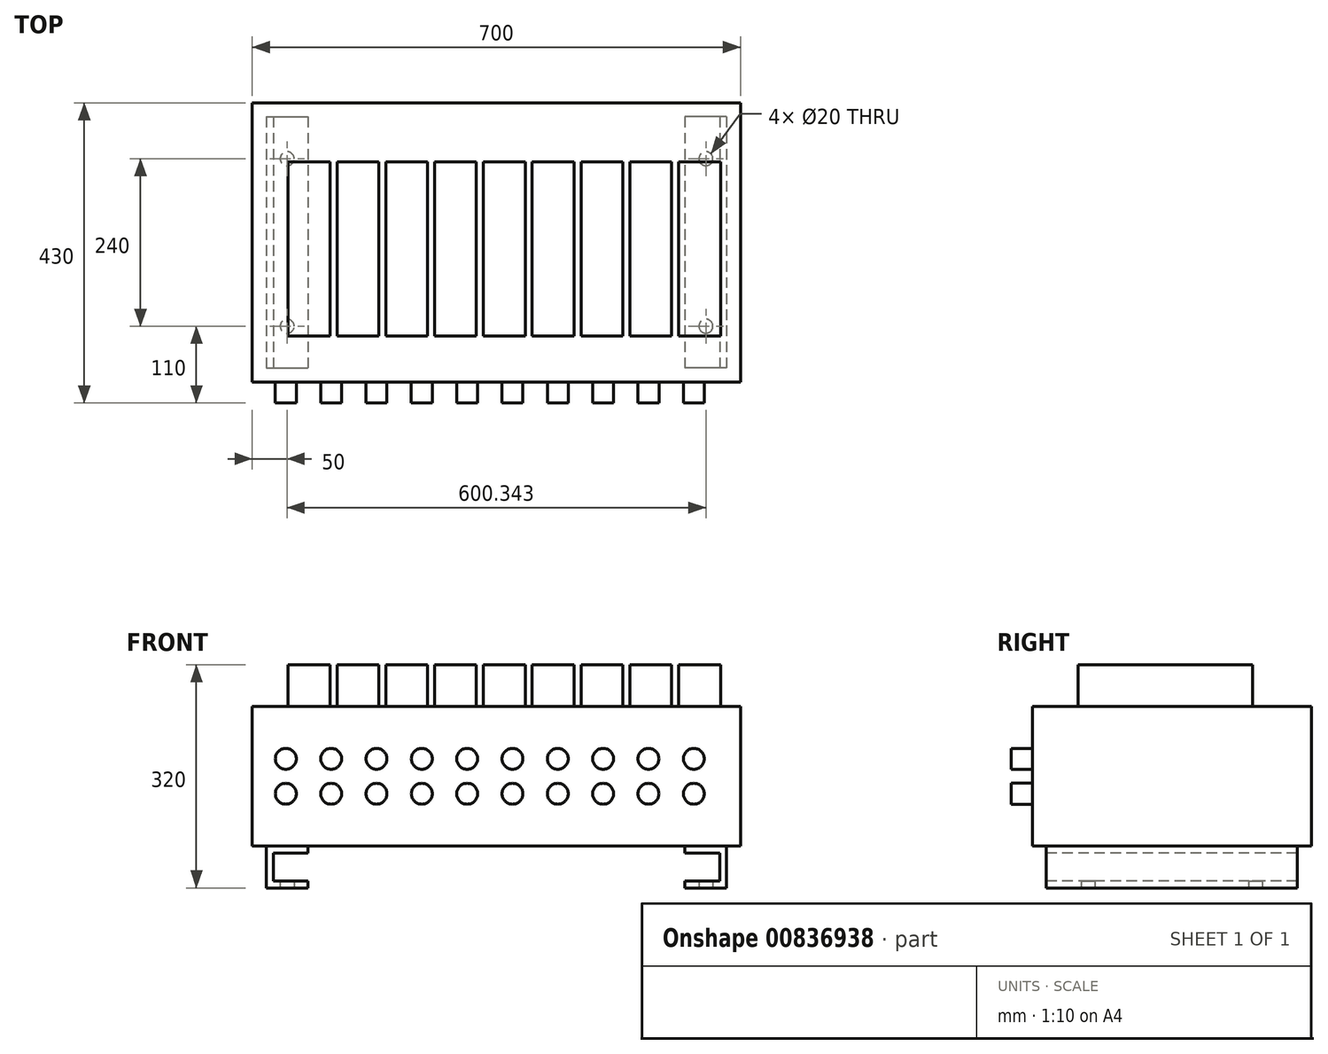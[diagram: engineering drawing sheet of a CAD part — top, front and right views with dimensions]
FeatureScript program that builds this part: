
annotation { "Feature Type Name" : "Feature", "Feature Type Description" : "" }
export const myFeature = defineFeature(function(context is Context, id is Id, definition is map)
    precondition{}
    {
        {
            var Q0;
            Q0=qCreatedBy(makeId("Front.planeOp"),FACE);
            var sketch = newSketch(context, id + "F0", { "sketchPlane" : qUnion([Q0])});
            skLineSegment(sketch, "E0.bottom", {"start": v(0, 0) * mm, "end": v(700, 0) * mm});
            skLineSegment(sketch, "E0.top", {"start": v(0, 200) * mm, "end": v(700, 200) * mm});
            skLineSegment(sketch, "E0.left", {"start": v(0, 0) * mm, "end": v(0, 200) * mm});
            skLineSegment(sketch, "E0.right", {"start": v(700, 0) * mm, "end": v(700, 200) * mm});
            skSolve(sketch);
        }
        {
            var Q0;
            Q0=makeQuery(id+"F0.imprint","IMPRINT",FACE,{"disambiguationData":[TD([[makeQuery(id+"F0.imprint","IMPRINT",EDGE,{"derivedFrom":sQuery(id+"F0.wireOp",EDGE,"E0.bottom")}),1.0]])]});
            extrude(context, id + "F1", {"entities" : qUnion([Q0]), "oppositeDirection" : true, "depth" : 400 * mm, "offsetDistance" : 25 * mm});
        }
        {
            var Q0;
            Q0=qCreatedBy(makeId("Front.planeOp"),FACE);
            cPlane(context, id + "F2", {"entities" : qUnion([Q0]), "cplaneType" : CPlaneType.OFFSET, "offset" : 20 * mm, "oppositeDirection" : true, "width" : 150 * mm, "height" : 150 * mm});
        }
        {
            var Q0;
            Q0=qCreatedBy(id+"F2.planeOp",FACE);
            var sketch = newSketch(context, id + "F3", { "sketchPlane" : qUnion([Q0])});
            skLineSegment(sketch, "E1", {"start": v(20, -19.14) * mm, "end": v(20, 199.88) * mm});
            skLineSegment(sketch, "E2.bottom", {"start": v(20, 0) * mm, "end": v(80, 0) * mm});
            skLineSegment(sketch, "E2.top", {"start": v(30, -10) * mm, "end": v(80, -10) * mm});
            skLineSegment(sketch, "E2.left", {"start": v(20, 0) * mm, "end": v(20, -10) * mm});
            skLineSegment(sketch, "E2.right", {"start": v(80, 0) * mm, "end": v(80, -10) * mm});
            skLineSegment(sketch, "E3.top", {"start": v(20, -60) * mm, "end": v(30, -60) * mm});
            skLineSegment(sketch, "E3.left", {"start": v(20, -10) * mm, "end": v(20, -60) * mm});
            skLineSegment(sketch, "E3.right", {"start": v(30, -10) * mm, "end": v(30, -50) * mm});
            skLineSegment(sketch, "E4.bottom", {"start": v(20, -60) * mm, "end": v(80, -60) * mm});
            skLineSegment(sketch, "E4.top", {"start": v(30, -50) * mm, "end": v(80, -50) * mm});
            skLineSegment(sketch, "E4.left", {"start": v(20, -60) * mm, "end": v(20, -50) * mm});
            skLineSegment(sketch, "E4.right", {"start": v(80, -60) * mm, "end": v(80, -50) * mm});
            skLineSegment(sketch, "E5", {"start": v(0, 0) * mm, "end": v(0, -147) * mm, "construction": true});
            skLineSegment(sketch, "E6", {"start": v(0, -147) * mm, "end": v(700, -147) * mm, "construction": true});
            skLineSegment(sketch, "E7", {"start": v(350, -147) * mm, "end": v(350, -185.28) * mm, "construction": true});
            skLineSegment(sketch, "E8.MirrorCS", {"start": v(680, 0) * mm, "end": v(680, -10) * mm});
            skLineSegment(sketch, "E9.MirrorCS", {"start": v(680, -60) * mm, "end": v(670, -60) * mm});
            skLineSegment(sketch, "E10.MirrorCS", {"start": v(620, -60) * mm, "end": v(620, -50) * mm});
            skLineSegment(sketch, "E11.MirrorCS", {"start": v(620, 0) * mm, "end": v(620, -10) * mm});
            skLineSegment(sketch, "E12.MirrorCS", {"start": v(670, -50) * mm, "end": v(620, -50) * mm});
            skLineSegment(sketch, "E13.MirrorCS", {"start": v(680, -10) * mm, "end": v(680, -60) * mm});
            skLineSegment(sketch, "E14.MirrorCS", {"start": v(670, -10) * mm, "end": v(670, -50) * mm});
            skLineSegment(sketch, "E15.MirrorCS", {"start": v(670, -10) * mm, "end": v(620, -10) * mm});
            skLineSegment(sketch, "E16.MirrorCS", {"start": v(680, 0) * mm, "end": v(620, 0) * mm});
            skLineSegment(sketch, "E17.MirrorCS", {"start": v(680, -60) * mm, "end": v(620, -60) * mm});
            skPoint(sketch, "E18.orphan", {"position": v(680, -50) * mm});
            skLineSegment(sketch, "E19", {"start": v(50, -60) * mm, "end": v(50, -71.61) * mm, "construction": true});
            skSolve(sketch);
        }
        {
            var Q0;
            Q0=makeQuery(id+"F3.imprint","IMPRINT",FACE,{"disambiguationData":[TD([[makeQuery(id+"F3.imprint","IMPRINT",EDGE,{"derivedFrom":sQuery(id+"F3.wireOp",EDGE,"E2.bottom")}),-1.0]])]});
            var Q1;
            {var subQ1=sQuery(id+"F3.wireOp",EDGE,"E3.bottom");Q1=makeQuery(id+"F3.imprint","IMPRINT",FACE,{"disambiguationData":[TD([[makeQuery(id+"F3.imprint","IMPRINT",EDGE,{"derivedFrom":subQ1}),-1.0]])]});}
            var Q2;
            {var subQ5=sQuery(id+"F3.wireOp",EDGE,"E4.left");Q2=makeQuery(id+"F3.imprint","IMPRINT",FACE,{"disambiguationData":[TD([[makeQuery(id+"F3.imprint","IMPRINT",EDGE,{"derivedFrom":subQ5}),-1.0]])]});}
            var Q3;
            {var subQ5=sQuery(id+"F3.wireOp",EDGE,"E4.right");Q3=makeQuery(id+"F3.imprint","IMPRINT",FACE,{"disambiguationData":[TD([[makeQuery(id+"F3.imprint","IMPRINT",EDGE,{"derivedFrom":subQ5}),1.0]])]});}
            var Q4;
            {var subQ1=sQuery(id+"F3.wireOp",EDGE,"E8.MirrorCS");Q4=makeQuery(id+"F3.imprint","IMPRINT",FACE,{"disambiguationData":[TD([[makeQuery(id+"F3.imprint","IMPRINT",EDGE,{"derivedFrom":subQ1}),-1.0]])]});}
            var Q5;
            {var subQ0=sQuery(id+"F3.wireOp",EDGE,"E13.MirrorCS");var subQ1=sQuery(id+"F3.wireOp",EDGE,"E12.MirrorCS");var subQ2=makeQuery(id+"F3.imprint","INTERSECT",VERTEX,{"derivedFrom":[subQ1,subQ0]});Q5=makeQuery(id+"F3.imprint","IMPRINT",FACE,{"disambiguationData":[TD([[makeQuery(id+"F3.imprint","IMPRINT",EDGE,{"disambiguationData":[TD([[subQ2,-1.0]])],"derivedFrom":subQ1}),-1.0]])]});}
            var Q6;
            {var subQ0=sQuery(id+"F3.wireOp",EDGE,"E10.MirrorCS");Q6=makeQuery(id+"F3.imprint","IMPRINT",FACE,{"disambiguationData":[TD([[makeQuery(id+"F3.imprint","IMPRINT",EDGE,{"derivedFrom":subQ0}),-1.0]])]});}
            var Q7;
            {var subQ0=sQuery(id+"F3.wireOp",EDGE,"E13.MirrorCS");var subQ1=sQuery(id+"F3.wireOp",EDGE,"E12.MirrorCS");var subQ2=makeQuery(id+"F3.imprint","INTERSECT",VERTEX,{"derivedFrom":[subQ1,subQ0]});Q7=makeQuery(id+"F3.imprint","IMPRINT",FACE,{"disambiguationData":[TD([[makeQuery(id+"F3.imprint","IMPRINT",EDGE,{"disambiguationData":[TD([[subQ2,-1.0]])],"derivedFrom":subQ1}),1.0]])]});}
            extrude(context, id + "F4", {"entities" : qUnion([Q0, Q1, Q2, Q3, Q4, Q5, Q6, Q7]), "operationType" : NewBodyOperationType.ADD, "oppositeDirection" : true, "depth" : 360 * mm, "offsetDistance" : 25 * mm});
        }
        {
            var Q0;
            Q0=makeQuery(id+"F1.opExtrude","CAP_FACE",FACE,{"disambiguationData":[OSD([sQuery(id+"F0.wireOp",EDGE,"E0.bottom"),sQuery(id+"F0.wireOp",EDGE,"E0.top"),sQuery(id+"F0.wireOp",EDGE,"E0.left"),sQuery(id+"F0.wireOp",EDGE,"E0.right")])],"isStart":true});
            var sketch = newSketch(context, id + "F5", { "sketchPlane" : qUnion([Q0])});
            skLineSegment(sketch, "E20", {"start": v(-69.57, 125) * mm, "end": v(743.33, 125) * mm});
            skLineSegment(sketch, "E21", {"start": v(-138.17, 34.89) * mm, "end": v(750.4, 34.89) * mm});
            skLineSegment(sketch, "E22", {"start": v(48.03, -83.74) * mm, "end": v(48.03, 302.08) * mm});
            skCircle(sketch, "E23", {"center": v(48.03, 125) * mm, "radius": 15 * mm});
            skCircle(sketch, "E24.0.1.0", {"center": v(48.03, 75) * mm, "radius": 15 * mm});
            skCircle(sketch, "E24.1.0.0", {"center": v(113.03, 125) * mm, "radius": 15 * mm});
            skCircle(sketch, "E24.1.1.0", {"center": v(113.03, 75) * mm, "radius": 15 * mm});
            skCircle(sketch, "E24.2.0.0", {"center": v(178.03, 125) * mm, "radius": 15 * mm});
            skCircle(sketch, "E24.2.1.0", {"center": v(178.03, 75) * mm, "radius": 15 * mm});
            skCircle(sketch, "E24.3.0.0", {"center": v(243.03, 125) * mm, "radius": 15 * mm});
            skCircle(sketch, "E24.3.1.0", {"center": v(243.03, 75) * mm, "radius": 15 * mm});
            skCircle(sketch, "E24.4.0.0", {"center": v(308.03, 125) * mm, "radius": 15 * mm});
            skCircle(sketch, "E24.4.1.0", {"center": v(308.03, 75) * mm, "radius": 15 * mm});
            skCircle(sketch, "E24.5.0.0", {"center": v(373.03, 125) * mm, "radius": 15 * mm});
            skCircle(sketch, "E24.5.1.0", {"center": v(373.03, 75) * mm, "radius": 15 * mm});
            skCircle(sketch, "E24.6.0.0", {"center": v(438.03, 125) * mm, "radius": 15 * mm});
            skCircle(sketch, "E24.6.1.0", {"center": v(438.03, 75) * mm, "radius": 15 * mm});
            skCircle(sketch, "E24.7.0.0", {"center": v(503.03, 125) * mm, "radius": 15 * mm});
            skCircle(sketch, "E24.7.1.0", {"center": v(503.03, 75) * mm, "radius": 15 * mm});
            skCircle(sketch, "E24.8.0.0", {"center": v(568.03, 125) * mm, "radius": 15 * mm});
            skCircle(sketch, "E24.8.1.0", {"center": v(568.03, 75) * mm, "radius": 15 * mm});
            skCircle(sketch, "E24.9.0.0", {"center": v(633.03, 125) * mm, "radius": 15 * mm});
            skCircle(sketch, "E24.9.1.0", {"center": v(633.03, 75) * mm, "radius": 15 * mm});
            skLineSegment(sketch, "E24.direction1", {"start": v(48.03, 125) * mm, "end": v(113.03, 125) * mm, "construction": true});
            skLineSegment(sketch, "E24.direction2", {"start": v(48.03, 125) * mm, "end": v(48.03, 75) * mm, "construction": true});
            skSolve(sketch);
        }
        {
            var Q0;
            Q0 = qSketchRegion(id + "F5", true);
            extrude(context, id + "F6", {"entities" : qUnion([Q0]), "operationType" : NewBodyOperationType.ADD, "depth" : 30 * mm, "offsetDistance" : 25 * mm});
        }
        {
            var Q0;
            Q0=makeQuery(id+"F1.opExtrude","SWEPT_FACE",FACE,{"disambiguationData":[OSD([sQuery(id+"F0.wireOp",EDGE,"E0.top")])]});
            var sketch = newSketch(context, id + "F7", { "sketchPlane" : qUnion([Q0])});
            skLineSegment(sketch, "E25.bottom", {"start": v(51.34, 315.72) * mm, "end": v(111.34, 315.72) * mm});
            skLineSegment(sketch, "E25.top", {"start": v(51.34, 65.72) * mm, "end": v(111.34, 65.72) * mm});
            skLineSegment(sketch, "E25.left", {"start": v(51.34, 315.72) * mm, "end": v(51.34, 65.72) * mm});
            skLineSegment(sketch, "E25.right", {"start": v(111.34, 315.72) * mm, "end": v(111.34, 65.72) * mm});
            skLineSegment(sketch, "E26.1.0.0", {"start": v(121.34, 65.72) * mm, "end": v(181.34, 65.72) * mm});
            skLineSegment(sketch, "E26.1.0.1", {"start": v(121.34, 315.72) * mm, "end": v(121.34, 65.72) * mm});
            skLineSegment(sketch, "E26.1.0.2", {"start": v(121.34, 315.72) * mm, "end": v(181.34, 315.72) * mm});
            skLineSegment(sketch, "E26.1.0.3", {"start": v(181.34, 315.72) * mm, "end": v(181.34, 65.72) * mm});
            skLineSegment(sketch, "E26.2.0.0", {"start": v(191.34, 65.72) * mm, "end": v(251.34, 65.72) * mm});
            skLineSegment(sketch, "E26.2.0.1", {"start": v(191.34, 315.72) * mm, "end": v(191.34, 65.72) * mm});
            skLineSegment(sketch, "E26.2.0.2", {"start": v(191.34, 315.72) * mm, "end": v(251.34, 315.72) * mm});
            skLineSegment(sketch, "E26.2.0.3", {"start": v(251.34, 315.72) * mm, "end": v(251.34, 65.72) * mm});
            skLineSegment(sketch, "E26.3.0.0", {"start": v(261.34, 65.72) * mm, "end": v(321.34, 65.72) * mm});
            skLineSegment(sketch, "E26.3.0.1", {"start": v(261.34, 315.72) * mm, "end": v(261.34, 65.72) * mm});
            skLineSegment(sketch, "E26.3.0.2", {"start": v(261.34, 315.72) * mm, "end": v(321.34, 315.72) * mm});
            skLineSegment(sketch, "E26.3.0.3", {"start": v(321.34, 315.72) * mm, "end": v(321.34, 65.72) * mm});
            skLineSegment(sketch, "E26.4.0.0", {"start": v(331.34, 65.72) * mm, "end": v(391.34, 65.72) * mm});
            skLineSegment(sketch, "E26.4.0.1", {"start": v(331.34, 315.72) * mm, "end": v(331.34, 65.72) * mm});
            skLineSegment(sketch, "E26.4.0.2", {"start": v(331.34, 315.72) * mm, "end": v(391.34, 315.72) * mm});
            skLineSegment(sketch, "E26.4.0.3", {"start": v(391.34, 315.72) * mm, "end": v(391.34, 65.72) * mm});
            skLineSegment(sketch, "E26.5.0.0", {"start": v(401.34, 65.72) * mm, "end": v(461.34, 65.72) * mm});
            skLineSegment(sketch, "E26.5.0.1", {"start": v(401.34, 315.72) * mm, "end": v(401.34, 65.72) * mm});
            skLineSegment(sketch, "E26.5.0.2", {"start": v(401.34, 315.72) * mm, "end": v(461.34, 315.72) * mm});
            skLineSegment(sketch, "E26.5.0.3", {"start": v(461.34, 315.72) * mm, "end": v(461.34, 65.72) * mm});
            skLineSegment(sketch, "E26.6.0.0", {"start": v(471.34, 65.72) * mm, "end": v(531.34, 65.72) * mm});
            skLineSegment(sketch, "E26.6.0.1", {"start": v(471.34, 315.72) * mm, "end": v(471.34, 65.72) * mm});
            skLineSegment(sketch, "E26.6.0.2", {"start": v(471.34, 315.72) * mm, "end": v(531.34, 315.72) * mm});
            skLineSegment(sketch, "E26.6.0.3", {"start": v(531.34, 315.72) * mm, "end": v(531.34, 65.72) * mm});
            skLineSegment(sketch, "E26.7.0.0", {"start": v(541.34, 65.72) * mm, "end": v(601.34, 65.72) * mm});
            skLineSegment(sketch, "E26.7.0.1", {"start": v(541.34, 315.72) * mm, "end": v(541.34, 65.72) * mm});
            skLineSegment(sketch, "E26.7.0.2", {"start": v(541.34, 315.72) * mm, "end": v(601.34, 315.72) * mm});
            skLineSegment(sketch, "E26.7.0.3", {"start": v(601.34, 315.72) * mm, "end": v(601.34, 65.72) * mm});
            skLineSegment(sketch, "E26.8.0.0", {"start": v(611.34, 65.72) * mm, "end": v(671.34, 65.72) * mm});
            skLineSegment(sketch, "E26.8.0.1", {"start": v(611.34, 315.72) * mm, "end": v(611.34, 65.72) * mm});
            skLineSegment(sketch, "E26.8.0.2", {"start": v(611.34, 315.72) * mm, "end": v(671.34, 315.72) * mm});
            skLineSegment(sketch, "E26.8.0.3", {"start": v(671.34, 315.72) * mm, "end": v(671.34, 65.72) * mm});
            skLineSegment(sketch, "E26.direction1", {"start": v(51.34, 65.72) * mm, "end": v(121.34, 65.72) * mm, "construction": true});
            skSolve(sketch);
        }
        {
            var Q0;
            Q0=makeQuery(id+"F7.imprint","IMPRINT",FACE,{"disambiguationData":[TD([[makeQuery(id+"F7.imprint","IMPRINT",EDGE,{"derivedFrom":sQuery(id+"F7.wireOp",EDGE,"E25.bottom")}),-1.0]])]});
            var Q1;
            Q1=makeQuery(id+"F7.imprint","IMPRINT",FACE,{"disambiguationData":[TD([[makeQuery(id+"F7.imprint","IMPRINT",EDGE,{"derivedFrom":sQuery(id+"F7.wireOp",EDGE,"E26.1.0.0")}),1.0]])]});
            var Q2;
            Q2=makeQuery(id+"F7.imprint","IMPRINT",FACE,{"disambiguationData":[TD([[makeQuery(id+"F7.imprint","IMPRINT",EDGE,{"derivedFrom":sQuery(id+"F7.wireOp",EDGE,"E26.2.0.0")}),1.0]])]});
            var Q3;
            Q3=makeQuery(id+"F7.imprint","IMPRINT",FACE,{"disambiguationData":[TD([[makeQuery(id+"F7.imprint","IMPRINT",EDGE,{"derivedFrom":sQuery(id+"F7.wireOp",EDGE,"E26.3.0.0")}),1.0]])]});
            var Q4;
            Q4=makeQuery(id+"F7.imprint","IMPRINT",FACE,{"disambiguationData":[TD([[makeQuery(id+"F7.imprint","IMPRINT",EDGE,{"derivedFrom":sQuery(id+"F7.wireOp",EDGE,"E26.4.0.0")}),1.0]])]});
            var Q5;
            Q5=makeQuery(id+"F7.imprint","IMPRINT",FACE,{"disambiguationData":[TD([[makeQuery(id+"F7.imprint","IMPRINT",EDGE,{"derivedFrom":sQuery(id+"F7.wireOp",EDGE,"E26.5.0.0")}),1.0]])]});
            var Q6;
            Q6=makeQuery(id+"F7.imprint","IMPRINT",FACE,{"disambiguationData":[TD([[makeQuery(id+"F7.imprint","IMPRINT",EDGE,{"derivedFrom":sQuery(id+"F7.wireOp",EDGE,"E26.6.0.0")}),1.0]])]});
            var Q7;
            Q7=makeQuery(id+"F7.imprint","IMPRINT",FACE,{"disambiguationData":[TD([[makeQuery(id+"F7.imprint","IMPRINT",EDGE,{"derivedFrom":sQuery(id+"F7.wireOp",EDGE,"E26.7.0.0")}),1.0]])]});
            var Q8;
            Q8=makeQuery(id+"F7.imprint","IMPRINT",FACE,{"disambiguationData":[TD([[makeQuery(id+"F7.imprint","IMPRINT",EDGE,{"derivedFrom":sQuery(id+"F7.wireOp",EDGE,"E26.8.0.0")}),1.0]])]});
            extrude(context, id + "F8", {"entities" : qUnion([Q0, Q1, Q2, Q3, Q4, Q5, Q6, Q7, Q8]), "operationType" : NewBodyOperationType.ADD, "depth" : 60 * mm, "offsetDistance" : 25 * mm});
        }
        {
            var Q0;
            Q0=makeQuery(id+"F4.opExtrude","SWEPT_FACE",FACE,{"disambiguationData":[OSD([sQuery(id+"F3.wireOp",EDGE,"E4.bottom")])]});
            var sketch = newSketch(context, id + "F9", { "sketchPlane" : qUnion([Q0])});
            skLineSegment(sketch, "E27", {"start": v(760.77, -80) * mm, "end": v(-99.12, -80) * mm, "construction": true});
            skLineSegment(sketch, "E28", {"start": v(50, -380) * mm, "end": v(50, 143.48) * mm});
            skLineSegment(sketch, "E29", {"start": v(50, -80) * mm, "end": v(20, -20) * mm, "construction": true});
            skCircle(sketch, "E30", {"center": v(50, -80) * mm, "radius": 10 * mm});
            skLineSegment(sketch, "E31", {"start": v(80, -200) * mm, "end": v(620.34, -200) * mm, "construction": true});
            skLineSegment(sketch, "E32", {"start": v(350.17, -200) * mm, "end": v(350.17, -437.74) * mm, "construction": true});
            skCircle(sketch, "E33.MirrorC", {"center": v(50, -320) * mm, "radius": 10 * mm});
            skCircle(sketch, "E34.MirrorC", {"center": v(650.34, -320) * mm, "radius": 10 * mm});
            skCircle(sketch, "E35.MirrorC", {"center": v(650.34, -80) * mm, "radius": 10 * mm});
            skSolve(sketch);
        }
        {
            var Q0;
            Q0 = qSketchRegion(id + "F9", true);
            extrude(context, id + "F10", {"entities" : qUnion([Q0]), "operationType" : NewBodyOperationType.REMOVE, "oppositeDirection" : true, "depth" : 25 * mm, "offsetDistance" : 25 * mm});
        }
    });
